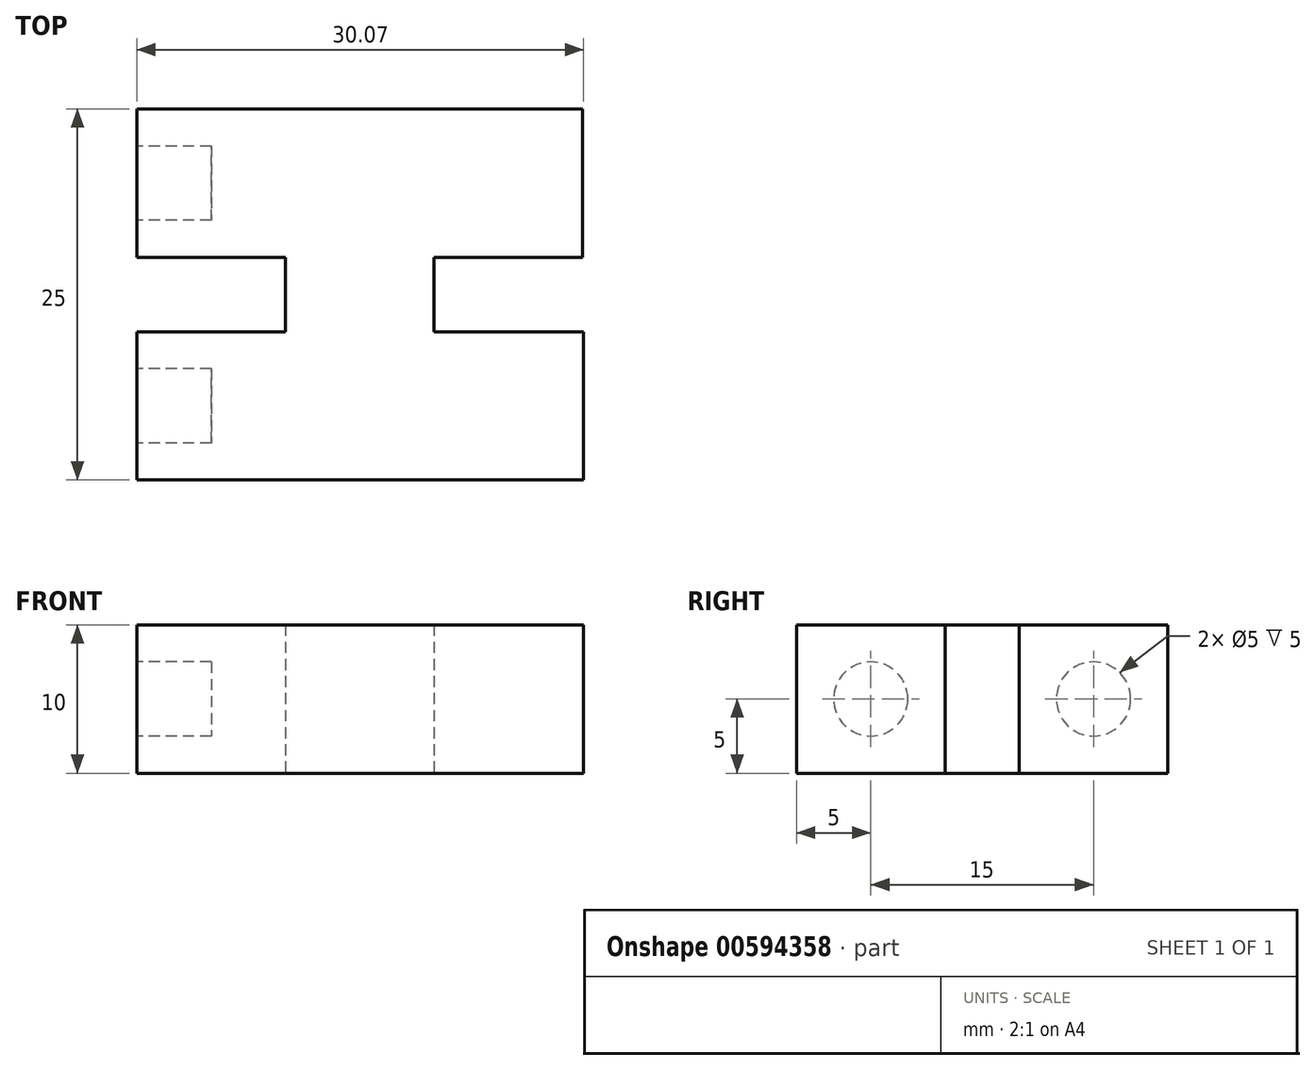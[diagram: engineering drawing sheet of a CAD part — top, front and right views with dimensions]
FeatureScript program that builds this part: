
annotation { "Feature Type Name" : "Feature", "Feature Type Description" : "" }
export const myFeature = defineFeature(function(context is Context, id is Id, definition is map)
    precondition{}
    {
        {
            var Q0;
            Q0=qCreatedBy(makeId("Top.planeOp"),FACE);
            var sketch = newSketch(context, id + "F0", { "sketchPlane" : qUnion([Q0])});
            skLineSegment(sketch, "E0", {"start": v(0, 0) * mm, "end": v(30, 0) * mm});
            skLineSegment(sketch, "E1", {"start": v(30, 0) * mm, "end": v(30, -10) * mm});
            skLineSegment(sketch, "E2", {"start": v(30, -10) * mm, "end": v(20, -10) * mm});
            skLineSegment(sketch, "E3", {"start": v(20, -10) * mm, "end": v(20, -15) * mm});
            skLineSegment(sketch, "E4", {"start": v(20, -15) * mm, "end": v(30.07, -15) * mm});
            skLineSegment(sketch, "E5", {"start": v(30.07, -15) * mm, "end": v(30.07, -25) * mm});
            skLineSegment(sketch, "E6", {"start": v(30.07, -25) * mm, "end": v(0, -25) * mm});
            skLineSegment(sketch, "E7", {"start": v(0, -25) * mm, "end": v(0, -15) * mm});
            skLineSegment(sketch, "E8", {"start": v(0, -15) * mm, "end": v(10, -15) * mm});
            skLineSegment(sketch, "E9", {"start": v(10, -15) * mm, "end": v(10, -10) * mm});
            skLineSegment(sketch, "E10", {"start": v(10, -10) * mm, "end": v(0, -10) * mm});
            skLineSegment(sketch, "E11", {"start": v(0, -10) * mm, "end": v(0, 0) * mm});
            skSolve(sketch);
        }
        {
            var Q0;
            Q0 = qSketchRegion(id + "F0", true);
            extrude(context, id + "F1", {"entities" : qUnion([Q0]), "depth" : 10 * mm, "offsetDistance" : 25 * mm});
        }
        {
            var Q0;
            Q0=makeQuery(id+"F1.opExtrude","SWEPT_FACE",FACE,{"disambiguationData":[OSD([sQuery(id+"F0.wireOp",EDGE,"E11")])]});
            cPlane(context, id + "F2", {"entities" : qUnion([Q0]), "cplaneType" : CPlaneType.OFFSET, "offset" : 0 * mm, "width" : 150 * mm, "height" : 150 * mm});
        }
        {
            var Q0;
            Q0=qCreatedBy(id+"F2.planeOp",FACE);
            var sketch = newSketch(context, id + "F3", { "sketchPlane" : qUnion([Q0])});
            skCircle(sketch, "E12", {"center": v(5, 5) * mm, "radius": 2.5 * mm});
            skCircle(sketch, "E13", {"center": v(20, 5) * mm, "radius": 2.5 * mm});
            skSolve(sketch);
        }
        {
            var Q0;
            Q0 = qSketchRegion(id + "F3", true);
            extrude(context, id + "F4", {"entities" : qUnion([Q0]), "operationType" : NewBodyOperationType.REMOVE, "oppositeDirection" : true, "depth" : 5 * mm, "offsetDistance" : 25 * mm});
        }
    });
